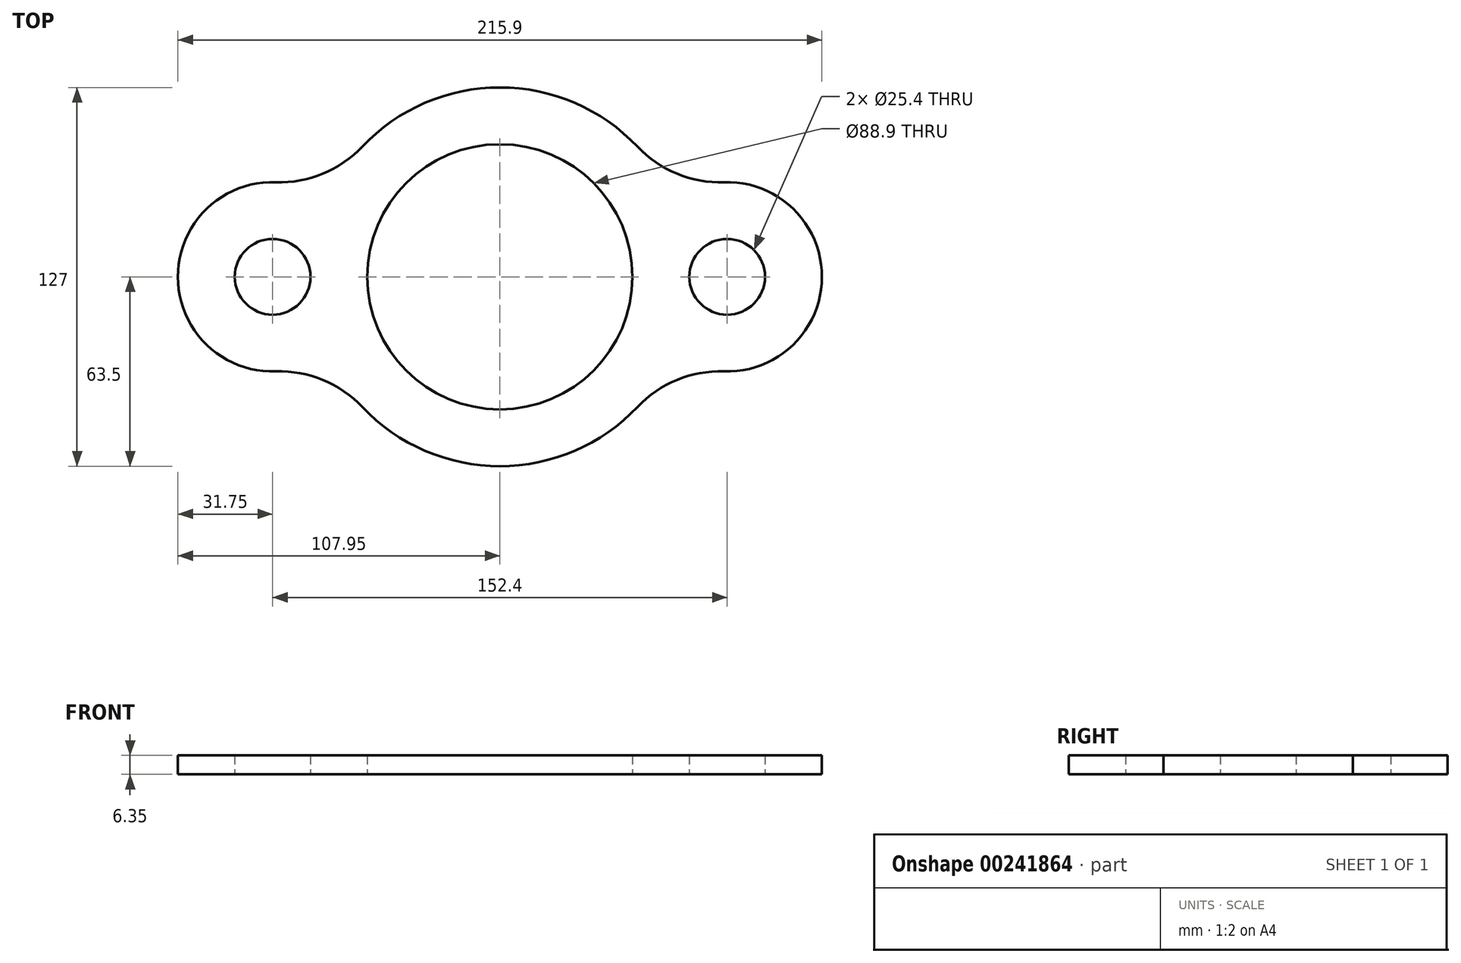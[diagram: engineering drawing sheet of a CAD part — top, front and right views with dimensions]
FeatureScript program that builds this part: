
annotation { "Feature Type Name" : "Feature", "Feature Type Description" : "" }
export const myFeature = defineFeature(function(context is Context, id is Id, definition is map)
    precondition{}
    {
        {
            var Q0;
            Q0=qCreatedBy(makeId("Top.planeOp"),FACE);
            var sketch = newSketch(context, id + "F0", { "sketchPlane" : qUnion([Q0])});
            skArc(sketch, "E0", {"start": v(-46.14, -43.63) * mm, "mid": v(0, -63.5) * mm, "end": v(46.14, -43.63) * mm});
            skCircle(sketch, "E1", {"center": v(0, 0) * mm, "radius": 44.45 * mm});
            skCircle(sketch, "E2", {"center": v(-76.2, 0) * mm, "radius": 12.7 * mm});
            skArc(sketch, "E3", {"start": v(75.12, -31.73) * mm, "mid": v(107.95, 0) * mm, "end": v(75.12, 31.73) * mm});
            skArc(sketch, "E4", {"start": v(-75.12, 31.73) * mm, "mid": v(-107.95, 0) * mm, "end": v(-75.12, -31.73) * mm});
            skCircle(sketch, "E5", {"center": v(76.2, 0) * mm, "radius": 12.7 * mm});
            skLineSegment(sketch, "E6", {"start": v(-76.2, 0) * mm, "end": v(0, 0) * mm});
            skLineSegment(sketch, "E7", {"start": v(0, 0) * mm, "end": v(76.2, 0) * mm});
            skArc(sketch, "E8.trimOffspring", {"start": v(46.14, 43.63) * mm, "mid": v(0, 63.5) * mm, "end": v(-46.14, 43.63) * mm});
            skPoint(sketch, "E9.visualSharp", {"position": v(-57.94, 25.98) * mm});
            skArc(sketch, "E9.filletArc", {"start": v(-75.12, 31.73) * mm, "mid": v(-59.35, 34.56) * mm, "end": v(-46.14, 43.63) * mm});
            skPoint(sketch, "E10.visualSharp", {"position": v(-57.94, -25.98) * mm});
            skArc(sketch, "E10.filletArc", {"start": v(-46.14, -43.63) * mm, "mid": v(-59.35, -34.56) * mm, "end": v(-75.12, -31.73) * mm});
            skPoint(sketch, "E11.visualSharp", {"position": v(57.94, 25.98) * mm});
            skArc(sketch, "E11.filletArc", {"start": v(46.14, 43.63) * mm, "mid": v(59.35, 34.56) * mm, "end": v(75.12, 31.73) * mm});
            skPoint(sketch, "E12.visualSharp", {"position": v(57.94, -25.98) * mm});
            skArc(sketch, "E12.filletArc", {"start": v(75.12, -31.73) * mm, "mid": v(59.35, -34.56) * mm, "end": v(46.14, -43.63) * mm});
            skSolve(sketch);
        }
        {
            var Q0;
            Q0 = qSketchRegion(id + "F0", true);
            extrude(context, id + "F1", {"entities" : qUnion([Q0]), "depth" : 6.35 * mm});
        }
    });
